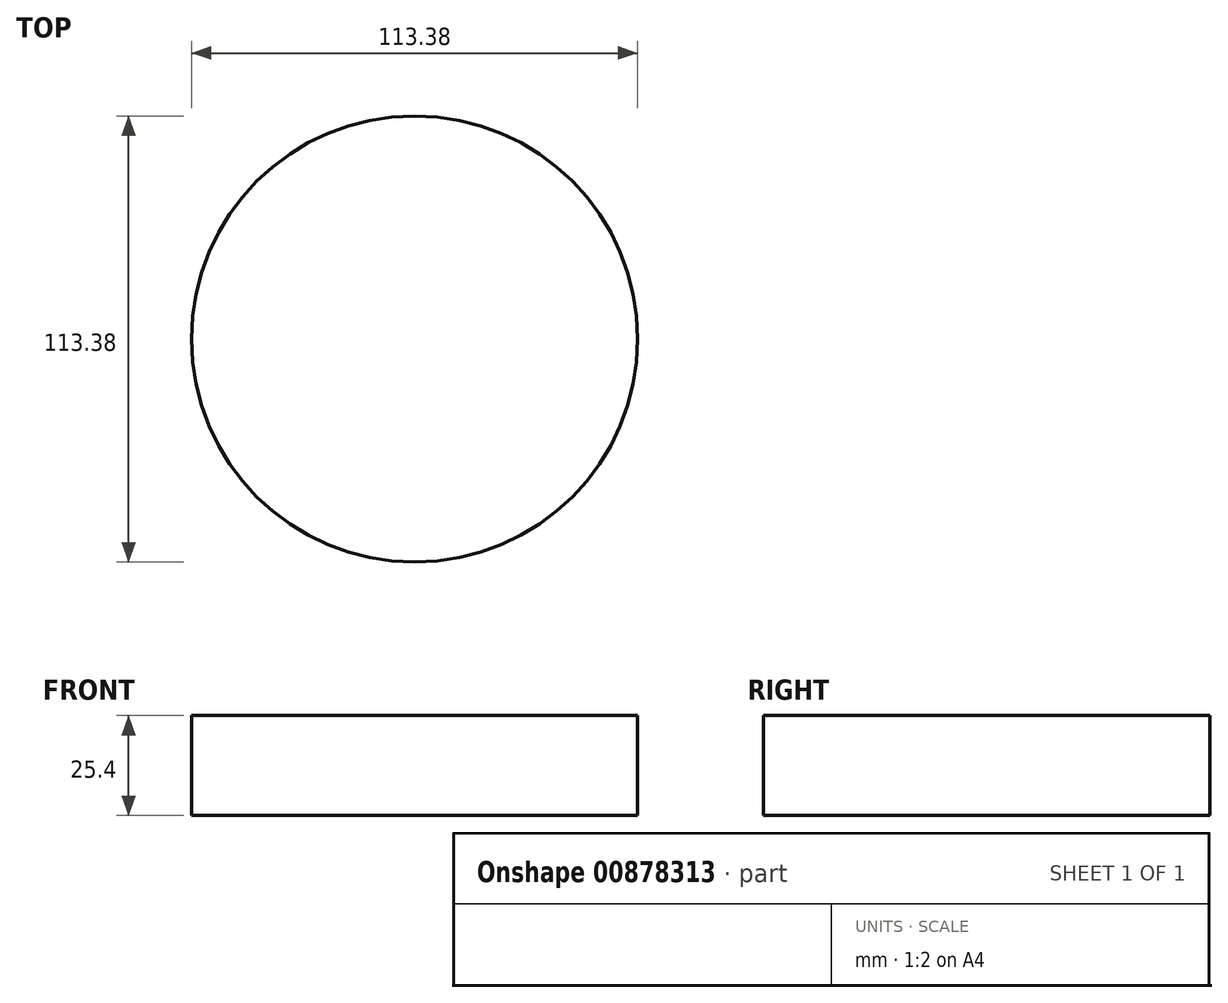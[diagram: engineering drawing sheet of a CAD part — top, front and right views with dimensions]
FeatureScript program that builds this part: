
annotation { "Feature Type Name" : "Feature", "Feature Type Description" : "" }
export const myFeature = defineFeature(function(context is Context, id is Id, definition is map)
    precondition{}
    {
        {
            var Q0;
            Q0=qCreatedBy(makeId("Top.planeOp"),FACE);
            var sketch = newSketch(context, id + "F0", { "sketchPlane" : qUnion([Q0])});
            skCircle(sketch, "E0", {"center": v(0, 13.73) * mm, "radius": 56.69 * mm});
            skSolve(sketch);
        }
        {
            var Q0;
            Q0=makeQuery(id+"F0.imprint","IMPRINT",FACE,{"disambiguationData":[TD([[makeQuery(id+"F0.imprint","IMPRINT",EDGE,{"derivedFrom":sQuery(id+"F0.wireOp",EDGE,"E0")}),1.0]])]});
            extrude(context, id + "F1", {"entities" : qUnion([Q0]), "depth" : 25.4 * mm, "offsetDistance" : 25.4 * mm});
        }
    });
